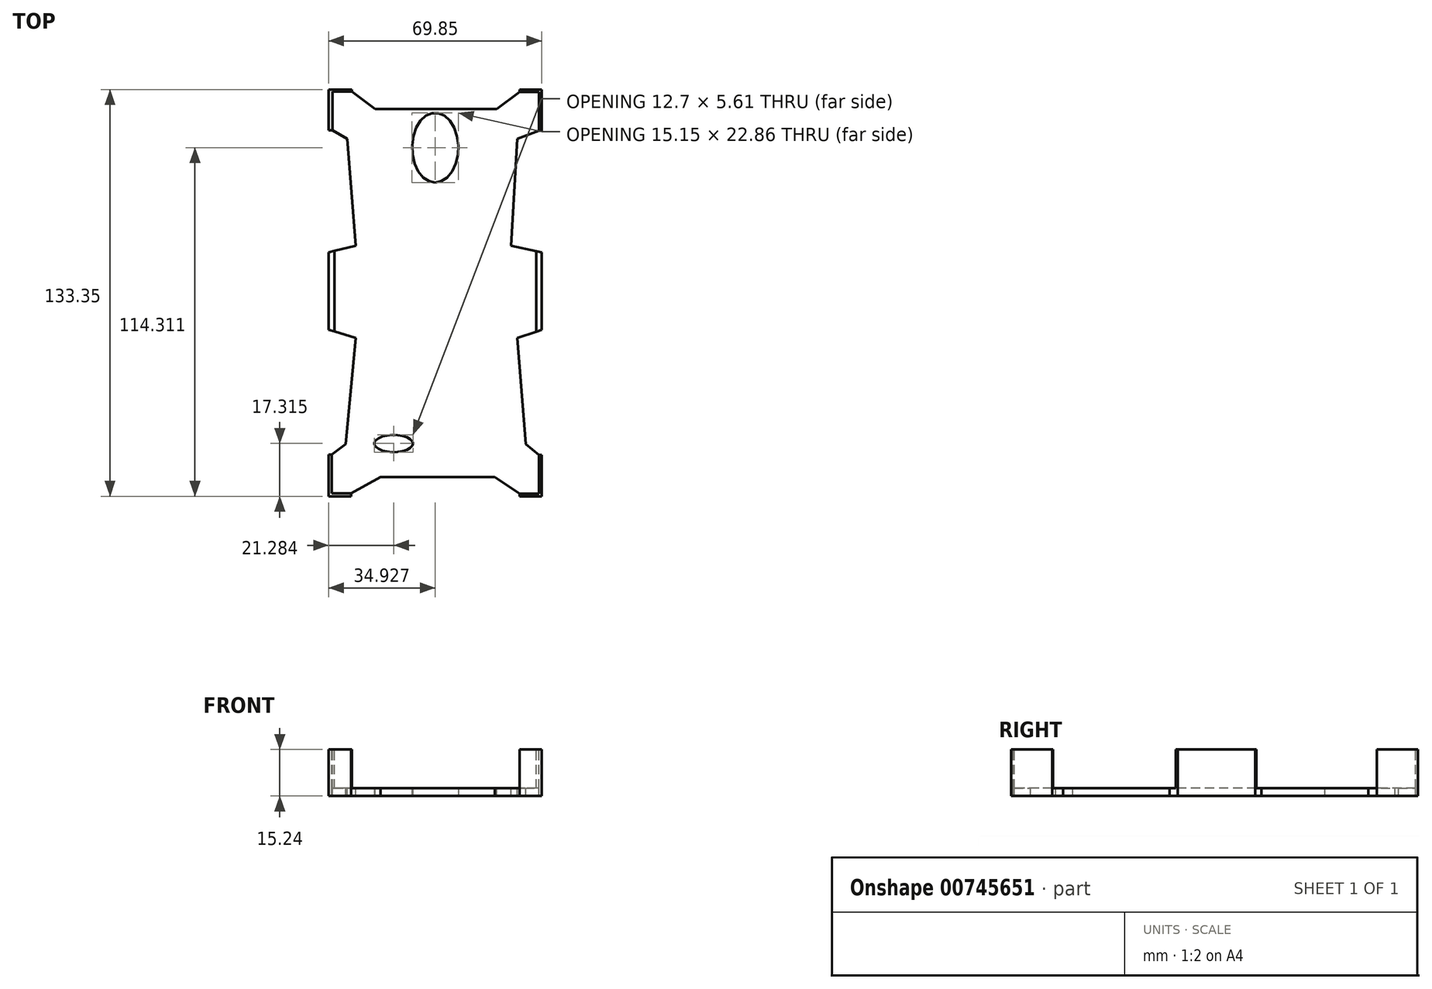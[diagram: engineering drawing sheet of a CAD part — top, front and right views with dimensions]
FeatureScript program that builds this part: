
annotation { "Feature Type Name" : "Feature", "Feature Type Description" : "" }
export const myFeature = defineFeature(function(context is Context, id is Id, definition is map)
    precondition{}
    {
        {
            var Q0;
            Q0=qCreatedBy(makeId("Top.planeOp"),FACE);
            var sketch = newSketch(context, id + "F0", { "sketchPlane" : qUnion([Q0])});
            skLineSegment(sketch, "E0.bottom", {"start": v(-39.84, 63.4) * mm, "end": v(30.01, 63.4) * mm});
            skLineSegment(sketch, "E0.top", {"start": v(-39.84, -69.94) * mm, "end": v(30.01, -69.94) * mm});
            skLineSegment(sketch, "E0.left", {"start": v(-39.84, 63.4) * mm, "end": v(-39.84, -69.94) * mm});
            skLineSegment(sketch, "E0.right", {"start": v(30.01, 63.4) * mm, "end": v(30.01, -69.94) * mm});
            skSolve(sketch);
        }
        {
            var Q0;
            Q0=makeQuery(id+"F0.imprint","IMPRINT",FACE,{"disambiguationData":[TD([[makeQuery(id+"F0.imprint","IMPRINT",EDGE,{"derivedFrom":sQuery(id+"F0.wireOp",EDGE,"E0.bottom")}),-1.0]])]});
            extrude(context, id + "F1", {"entities" : qUnion([Q0]), "depth" : 15.24 * mm, "offsetDistance" : 25.4 * mm});
        }
        {
            var Q0;
            Q0=makeQuery(id+"F1.opExtrude","CAP_FACE",FACE,{"disambiguationData":[OSD([sQuery(id+"F0.wireOp",EDGE,"E0.bottom"),sQuery(id+"F0.wireOp",EDGE,"E0.top"),sQuery(id+"F0.wireOp",EDGE,"E0.left"),sQuery(id+"F0.wireOp",EDGE,"E0.right")])],"isStart":false});
            var sketch = newSketch(context, id + "F2", { "sketchPlane" : qUnion([Q0])});
            skLineSegment(sketch, "E1", {"start": v(-39.84, 63.4) * mm, "end": v(-39.84, 50.7) * mm});
            skLineSegment(sketch, "E2", {"start": v(-39.84, 50.7) * mm, "end": v(-39.84, 10.07) * mm});
            skLineSegment(sketch, "E3", {"start": v(-39.84, 10.07) * mm, "end": v(-39.84, -15.33) * mm});
            skLineSegment(sketch, "E4", {"start": v(-39.84, -15.33) * mm, "end": v(-39.84, -55.97) * mm});
            skLineSegment(sketch, "E5", {"start": v(-39.84, -55.97) * mm, "end": v(-39.84, -69.94) * mm});
            skLineSegment(sketch, "E6", {"start": v(30.01, 63.4) * mm, "end": v(30.01, 50.7) * mm});
            skLineSegment(sketch, "E7", {"start": v(30.01, 50.7) * mm, "end": v(30.01, 10.07) * mm});
            skLineSegment(sketch, "E8", {"start": v(30.01, 10.07) * mm, "end": v(30.01, -15.33) * mm});
            skLineSegment(sketch, "E9", {"start": v(30.01, -15.33) * mm, "end": v(30.01, -55.97) * mm});
            skLineSegment(sketch, "E10", {"start": v(30.01, -55.97) * mm, "end": v(30.01, -69.94) * mm});
            skLineSegment(sketch, "E11", {"start": v(-33.69, 47.23) * mm, "end": v(-30.92, 12.16) * mm});
            skLineSegment(sketch, "E12", {"start": v(-30.92, 12.16) * mm, "end": v(-39.84, 10.07) * mm});
            skLineSegment(sketch, "E13", {"start": v(-39.84, -15.33) * mm, "end": v(-30.92, -18.02) * mm});
            skLineSegment(sketch, "E14", {"start": v(-30.92, -18.02) * mm, "end": v(-34.33, -52.88) * mm});
            skLineSegment(sketch, "E15", {"start": v(20, 12.16) * mm, "end": v(30.01, 10.07) * mm});
            skLineSegment(sketch, "E16", {"start": v(30.01, -15.33) * mm, "end": v(22, -18.02) * mm});
            skLineSegment(sketch, "E17", {"start": v(22, -18.02) * mm, "end": v(24.74, -52.88) * mm});
            skEllipse(sketch, "E18", {"center": v(-4.91, 44.37) * mm, "majorRadius": 11.43 * mm, "minorRadius": 7.58 * mm, "majorAxis": v(0, -1)});
            skPoint(sketch, "E18.centerSnap0", {"position": v(-4.91, -69.94) * mm});
            skLineSegment(sketch, "E19", {"start": v(-38, 10.5) * mm, "end": v(-38, -15.89) * mm});
            skLineSegment(sketch, "E20", {"start": v(28.19, 10.45) * mm, "end": v(28.19, -15.95) * mm});
            skLineSegment(sketch, "E21", {"start": v(-4.91, 63.4) * mm, "end": v(-4.91, 57.06) * mm});
            skLineSegment(sketch, "E22", {"start": v(-24.57, 57.06) * mm, "end": v(15.26, 57.06) * mm});
            skLineSegment(sketch, "E23", {"start": v(-6.86, -69.94) * mm, "end": v(-6.86, -63.6) * mm});
            skLineSegment(sketch, "E24", {"start": v(-22.8, -63.6) * mm, "end": v(14.6, -63.6) * mm});
            skLineSegment(sketch, "E25", {"start": v(-38.78, -56.21) * mm, "end": v(-38.78, -68.91) * mm});
            skLineSegment(sketch, "E26", {"start": v(-38.78, -68.91) * mm, "end": v(-32.43, -68.91) * mm});
            skLineSegment(sketch, "E27", {"start": v(29.08, -56.43) * mm, "end": v(29.08, -69.13) * mm});
            skLineSegment(sketch, "E28", {"start": v(29.08, -69.13) * mm, "end": v(22.73, -69.13) * mm});
            skLineSegment(sketch, "E29", {"start": v(-32.26, 62.72) * mm, "end": v(-38.6, 62.72) * mm});
            skLineSegment(sketch, "E30", {"start": v(-38.6, 62.72) * mm, "end": v(-38.6, 50.02) * mm});
            skEllipse(sketch, "E31", {"center": v(-18.56, -52.62) * mm, "majorRadius": 6.35 * mm, "minorRadius": 2.8 * mm, "majorAxis": v(1, 0)});
            skLineSegment(sketch, "E32", {"start": v(20, 12.16) * mm, "end": v(22.04, 47.23) * mm});
            skLineSegment(sketch, "E33", {"start": v(29.1, 62.67) * mm, "end": v(22.75, 62.67) * mm});
            skLineSegment(sketch, "E34", {"start": v(29.1, 62.67) * mm, "end": v(29.1, 49.97) * mm});
            skLineSegment(sketch, "E35", {"start": v(22.75, 62.67) * mm, "end": v(15.26, 57.06) * mm});
            skLineSegment(sketch, "E36", {"start": v(29.1, 49.97) * mm, "end": v(22.04, 47.23) * mm});
            skLineSegment(sketch, "E37", {"start": v(22.75, 62.67) * mm, "end": v(22.75, 63.4) * mm});
            skLineSegment(sketch, "E38", {"start": v(29.1, 49.97) * mm, "end": v(30.01, 49.97) * mm});
            skLineSegment(sketch, "E39", {"start": v(-24.57, 57.06) * mm, "end": v(-32.26, 62.72) * mm});
            skLineSegment(sketch, "E40", {"start": v(-33.69, 47.23) * mm, "end": v(-38.6, 50.02) * mm});
            skLineSegment(sketch, "E41", {"start": v(-38.6, 50.02) * mm, "end": v(-39.84, 50.02) * mm});
            skLineSegment(sketch, "E42", {"start": v(-32.26, 62.72) * mm, "end": v(-32.26, 63.4) * mm});
            skLineSegment(sketch, "E43", {"start": v(-38.78, -56.21) * mm, "end": v(-34.33, -52.88) * mm});
            skLineSegment(sketch, "E44", {"start": v(-32.43, -68.91) * mm, "end": v(-22.8, -63.6) * mm});
            skLineSegment(sketch, "E45", {"start": v(-38.78, -56.21) * mm, "end": v(-39.84, -56.21) * mm});
            skLineSegment(sketch, "E46", {"start": v(-32.43, -68.91) * mm, "end": v(-32.43, -69.94) * mm});
            skLineSegment(sketch, "E47", {"start": v(29.08, -56.43) * mm, "end": v(24.74, -52.88) * mm});
            skLineSegment(sketch, "E48", {"start": v(22.73, -69.13) * mm, "end": v(14.6, -63.6) * mm});
            skLineSegment(sketch, "E49", {"start": v(22.73, -69.13) * mm, "end": v(22.73, -69.94) * mm});
            skLineSegment(sketch, "E50", {"start": v(29.08, -56.43) * mm, "end": v(30.01, -56.43) * mm});
            skSolve(sketch);
        }
        {
            var Q0;
            {var subQ3=sQuery(id+"F2.wireOp",EDGE,"E4");Q0=makeQuery(id+"F2.imprint","IMPRINT",FACE,{"disambiguationData":[TD([[makeQuery(id+"F2.imprint","IMPRINT",EDGE,{"derivedFrom":subQ3}),1.0]])]});}
            var Q1;
            {var subQ1=sQuery(id+"F2.wireOp",EDGE,"E2");Q1=makeQuery(id+"F2.imprint","IMPRINT",FACE,{"disambiguationData":[TD([[makeQuery(id+"F2.imprint","IMPRINT",EDGE,{"derivedFrom":subQ1}),1.0]])]});}
            var Q2;
            {var subQ5=sQuery(id+"F2.wireOp",EDGE,"E21");Q2=makeQuery(id+"F2.imprint","IMPRINT",FACE,{"disambiguationData":[TD([[makeQuery(id+"F2.imprint","IMPRINT",EDGE,{"derivedFrom":subQ5}),1.0]])]});}
            var Q3;
            {var subQ1=sQuery(id+"F2.wireOp",EDGE,"E21");Q3=makeQuery(id+"F2.imprint","IMPRINT",FACE,{"disambiguationData":[TD([[makeQuery(id+"F2.imprint","IMPRINT",EDGE,{"derivedFrom":subQ1}),-1.0]])]});}
            var Q4;
            {var subQ2=sQuery(id+"F2.wireOp",EDGE,"E7");Q4=makeQuery(id+"F2.imprint","IMPRINT",FACE,{"disambiguationData":[TD([[makeQuery(id+"F2.imprint","IMPRINT",EDGE,{"derivedFrom":subQ2}),-1.0]])]});}
            var Q5;
            {var subQ3=sQuery(id+"F2.wireOp",EDGE,"E9");Q5=makeQuery(id+"F2.imprint","IMPRINT",FACE,{"disambiguationData":[TD([[makeQuery(id+"F2.imprint","IMPRINT",EDGE,{"derivedFrom":subQ3}),-1.0]])]});}
            var Q6;
            {var subQ1=sQuery(id+"F2.wireOp",EDGE,"E23");Q6=makeQuery(id+"F2.imprint","IMPRINT",FACE,{"disambiguationData":[TD([[makeQuery(id+"F2.imprint","IMPRINT",EDGE,{"derivedFrom":subQ1}),1.0]])]});}
            var Q7;
            {var subQ5=sQuery(id+"F2.wireOp",EDGE,"E23");Q7=makeQuery(id+"F2.imprint","IMPRINT",FACE,{"disambiguationData":[TD([[makeQuery(id+"F2.imprint","IMPRINT",EDGE,{"derivedFrom":subQ5}),-1.0]])]});}
            extrude(context, id + "F3", {"entities" : qUnion([Q0, Q1, Q2, Q3, Q4, Q5, Q6, Q7]), "operationType" : NewBodyOperationType.REMOVE, "endBound" : BoundingType.THROUGH_ALL, "oppositeDirection" : true, "depth" : 25.4 * mm, "offsetDistance" : 25.4 * mm});
        }
        {
            var Q0;
            Q0=makeQuery(id+"F2.imprint","IMPRINT",FACE,{"disambiguationData":[TD([[makeQuery(id+"F2.imprint","IMPRINT",EDGE,{"derivedFrom":sQuery(id+"F2.wireOp",EDGE,"E18")}),1.0]])]});
            var Q1;
            Q1=makeQuery(id+"F2.imprint","IMPRINT",FACE,{"disambiguationData":[TD([[makeQuery(id+"F2.imprint","IMPRINT",EDGE,{"derivedFrom":sQuery(id+"F2.wireOp",EDGE,"npgbGc0a-Nooc-pZsI-Jwf4-jJlvZ8AxyBd8")}),1.0]])]});
            extrude(context, id + "F4", {"entities" : qUnion([Q0, Q1]), "operationType" : NewBodyOperationType.REMOVE, "endBound" : BoundingType.THROUGH_ALL, "oppositeDirection" : true, "depth" : 25.4 * mm, "offsetDistance" : 25.4 * mm});
        }
        {
            var Q0;
            {var subQ17=sQuery(id+"F2.wireOp",EDGE,"E11");Q0=makeQuery(id+"F2.imprint","IMPRINT",FACE,{"disambiguationData":[TD([[makeQuery(id+"F2.imprint","IMPRINT",EDGE,{"derivedFrom":subQ17}),1.0]])]});}
            extrude(context, id + "F5", {"entities" : qUnion([Q0]), "operationType" : NewBodyOperationType.REMOVE, "oppositeDirection" : true, "depth" : 12.7 * mm, "offsetDistance" : 25.4 * mm});
        }
        {
            var Q0;
            Q0=makeQuery(id+"F5.boolean.opBoolean","SPLIT",FACE,{"disambiguationData":[TD([makeQuery(id+"F5.opExtrude","SWEPT_FACE",FACE,{"disambiguationData":[OSD([sQuery(id+"F2.wireOp",EDGE,"E31")])]})])],"derivedFrom":makeQuery(id+"F1.opExtrude","CAP_FACE",FACE,{"disambiguationData":[OSD([sQuery(id+"F0.wireOp",EDGE,"E0.bottom"),sQuery(id+"F0.wireOp",EDGE,"E0.top"),sQuery(id+"F0.wireOp",EDGE,"E0.left"),sQuery(id+"F0.wireOp",EDGE,"E0.right")])],"isStart":false})});
            extrude(context, id + "F6", {"entities" : qUnion([Q0]), "operationType" : NewBodyOperationType.REMOVE, "endBound" : BoundingType.THROUGH_ALL, "oppositeDirection" : true, "depth" : 25.4 * mm, "offsetDistance" : 25.4 * mm});
        }
    });
